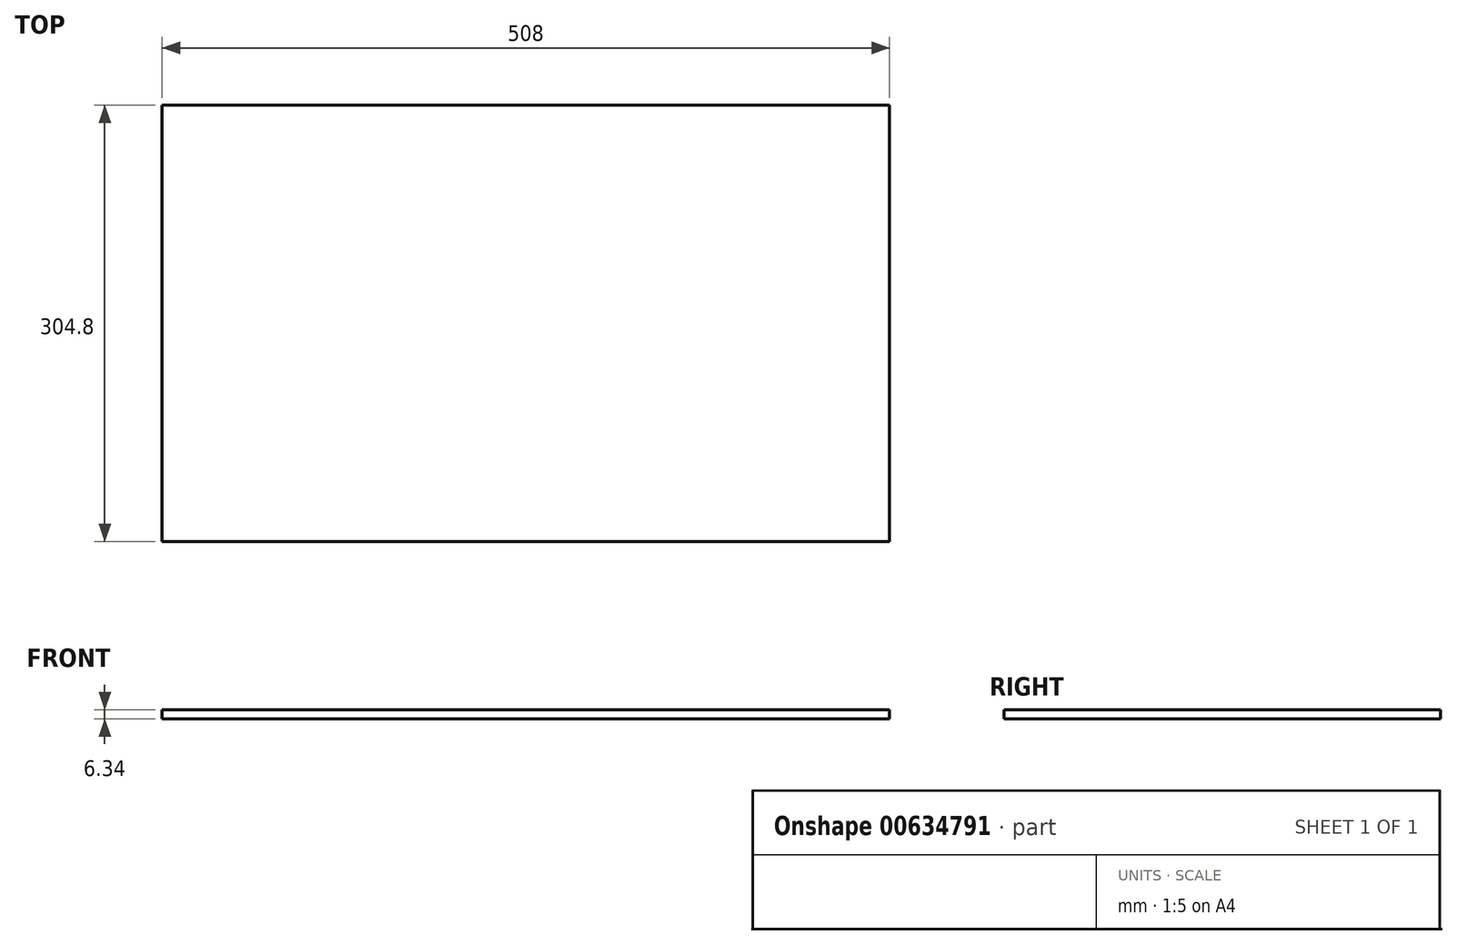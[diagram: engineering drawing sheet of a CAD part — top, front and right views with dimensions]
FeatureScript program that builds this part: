
annotation { "Feature Type Name" : "Feature", "Feature Type Description" : "" }
export const myFeature = defineFeature(function(context is Context, id is Id, definition is map)
    precondition{}
    {
        {
            var Q0;
            Q0=qCreatedBy(makeId("Front.planeOp"),FACE);
            var sketch = newSketch(context, id + "F0", { "sketchPlane" : qUnion([Q0])});
            skLineSegment(sketch, "E0.bottom", {"start": v(-254, 3.17) * mm, "end": v(254, 3.17) * mm});
            skLineSegment(sketch, "E0.top", {"start": v(-254, -3.18) * mm, "end": v(254, -3.18) * mm});
            skLineSegment(sketch, "E0.left", {"start": v(-254, 3.18) * mm, "end": v(-254, -3.18) * mm});
            skLineSegment(sketch, "E0.right", {"start": v(254, 3.18) * mm, "end": v(254, -3.18) * mm});
            skLineSegment(sketch, "E1", {"start": v(-254, 3.17) * mm, "end": v(254, -3.17) * mm, "construction": true});
            skSolve(sketch);
        }
        {
            var Q0;
            Q0 = qSketchRegion(id + "F0", true);
            extrude(context, id + "F1", {"entities" : qUnion([Q0]), "endBound" : BoundingType.SYMMETRIC, "depth" : 304.8 * mm, "offsetDistance" : 25.4 * mm});
        }
    });
